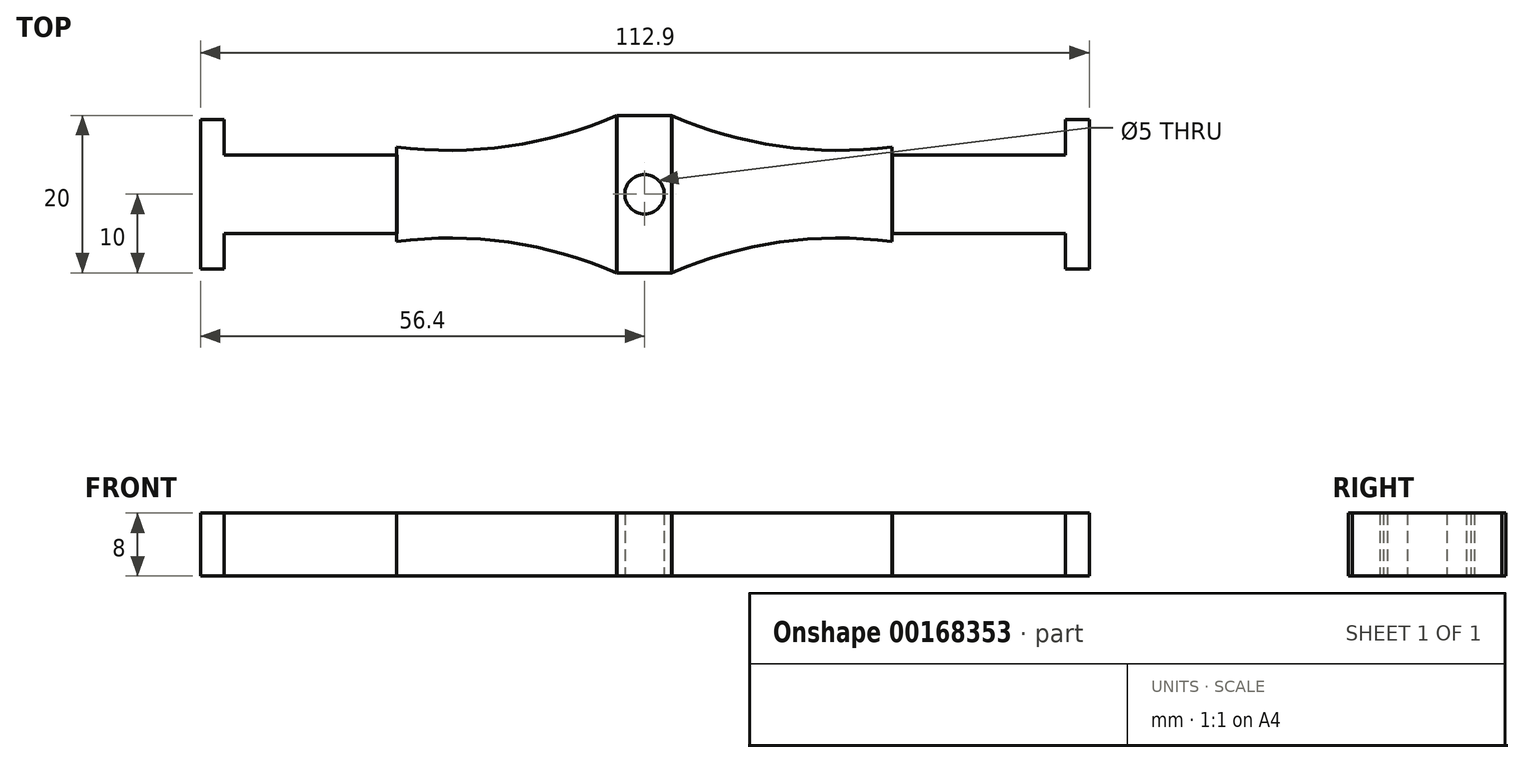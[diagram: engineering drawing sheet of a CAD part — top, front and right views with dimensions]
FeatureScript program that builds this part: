
annotation { "Feature Type Name" : "Feature", "Feature Type Description" : "" }
export const myFeature = defineFeature(function(context is Context, id is Id, definition is map)
    precondition{}
    {
        {
            var Q0;
            Q0=qCreatedBy(makeId("Top.planeOp"),FACE);
            var sketch = newSketch(context, id + "F0", { "sketchPlane" : qUnion([Q0])});
            skLineSegment(sketch, "E0.bottom", {"start": v(-3.5, 10) * mm, "end": v(3.5, 10) * mm});
            skLineSegment(sketch, "E0.top", {"start": v(-3.5, -10) * mm, "end": v(3.5, -10) * mm});
            skLineSegment(sketch, "E0.left", {"start": v(-3.5, 10) * mm, "end": v(-3.5, -10) * mm});
            skLineSegment(sketch, "E0.right", {"start": v(3.5, 10) * mm, "end": v(3.5, -10) * mm});
            skPoint(sketch, "E0.middle", {"position": v(0, 0) * mm});
            skLineSegment(sketch, "E1.bottom", {"start": v(-56.5, 9.5) * mm, "end": v(-53.5, 9.5) * mm});
            skLineSegment(sketch, "E1.top", {"start": v(-56.5, -9.5) * mm, "end": v(-53.5, -9.5) * mm});
            skLineSegment(sketch, "E1.left", {"start": v(-56.5, 9.5) * mm, "end": v(-56.5, -9.5) * mm});
            skLineSegment(sketch, "E1.right", {"start": v(-53.5, 9.5) * mm, "end": v(-53.5, -9.5) * mm});
            skPoint(sketch, "E1.middle", {"position": v(-55, 0) * mm});
            skLineSegment(sketch, "E2.left", {"start": v(-53.5, 4.03) * mm, "end": v(-53.5, -5.02) * mm});
            skLineSegment(sketch, "E3.bottom", {"start": v(-53.5, -5.02) * mm, "end": v(-31.5, -5.02) * mm});
            skLineSegment(sketch, "E3.top", {"start": v(-53.5, 4.98) * mm, "end": v(-31.5, 4.98) * mm});
            skLineSegment(sketch, "E3.left", {"start": v(-53.5, -5.02) * mm, "end": v(-53.5, 4.98) * mm});
            skLineSegment(sketch, "E3.right", {"start": v(-31.5, -5.02) * mm, "end": v(-31.5, 4.98) * mm});
            skLineSegment(sketch, "E4.MirrorCS", {"start": v(53.5, -5.02) * mm, "end": v(53.5, 4.98) * mm});
            skLineSegment(sketch, "E5.MirrorCS", {"start": v(53.5, 4.98) * mm, "end": v(31.5, 4.98) * mm});
            skLineSegment(sketch, "E6.MirrorCS", {"start": v(53.5, -5.02) * mm, "end": v(31.5, -5.02) * mm});
            skLineSegment(sketch, "E7.MirrorCS", {"start": v(31.5, -5.02) * mm, "end": v(31.5, 4.98) * mm});
            skCircle(sketch, "E8", {"center": v(0, 0) * mm, "radius": 2.5 * mm});
            skLineSegment(sketch, "E9", {"start": v(0, 24.62) * mm, "end": v(0, -21.09) * mm});
            skLineSegment(sketch, "E10.MirrorCS", {"start": v(53.5, 9.5) * mm, "end": v(53.5, -9.5) * mm});
            skLineSegment(sketch, "E11.MirrorCS", {"start": v(56.5, 9.5) * mm, "end": v(53.5, 9.5) * mm});
            skLineSegment(sketch, "E12.MirrorCS", {"start": v(56.5, 9.5) * mm, "end": v(56.5, -9.5) * mm});
            skLineSegment(sketch, "E13.MirrorCS", {"start": v(56.5, -9.5) * mm, "end": v(53.5, -9.5) * mm});
            skSolve(sketch);
        }
        {
            var Q0;
            Q0 = qSketchRegion(id + "F0", true);
            var Q1;
            {var subQ4=sQuery(id+"F0.wireOp",EDGE,"E3.bottom");Q1=makeQuery(id+"F0.imprint","IMPRINT",FACE,{"disambiguationData":[TD([[makeQuery(id+"F0.imprint","IMPRINT",EDGE,{"derivedFrom":subQ4}),1.0]])]});}
            extrude(context, id + "F1", {"entities" : qUnion([Q0, Q1]), "depth" : 8 * mm});
        }
        {
            var Q0;
            Q0=qCreatedBy(makeId("Top.planeOp"),FACE);
            var sketch = newSketch(context, id + "F2", { "sketchPlane" : qUnion([Q0])});
            skLineSegment(sketch, "E14", {"start": v(-31.51, 6) * mm, "end": v(-31.51, -6) * mm});
            skLineSegment(sketch, "E15", {"start": v(31.51, 6) * mm, "end": v(31.51, -6) * mm});
            skArc(sketch, "E16", {"start": v(-31.51, 6) * mm, "mid": v(-17.25, 6.1) * mm, "end": v(-3.54, 10) * mm});
            skPoint(sketch, "E17.endSnap0", {"position": v(31.51, 0) * mm});
            skArc(sketch, "E18.MirrorCS", {"start": v(-31.51, -6) * mm, "mid": v(-17.25, -6.1) * mm, "end": v(-3.54, -10) * mm});
            skArc(sketch, "E19.MirrorCS", {"start": v(31.51, 6) * mm, "mid": v(17.25, 6.1) * mm, "end": v(3.54, 10) * mm});
            skArc(sketch, "E20.MirrorCS", {"start": v(31.51, -6) * mm, "mid": v(17.25, -6.1) * mm, "end": v(3.54, -10) * mm});
            skLineSegment(sketch, "E21", {"start": v(-3.54, 10) * mm, "end": v(-3.54, -10) * mm});
            skLineSegment(sketch, "E22", {"start": v(3.54, 10) * mm, "end": v(3.54, -10) * mm});
            skSolve(sketch);
        }
        {
            var Q0;
            Q0=makeQuery(id+"F2.imprint","IMPRINT",FACE,{"disambiguationData":[TD([[makeQuery(id+"F2.imprint","IMPRINT",EDGE,{"derivedFrom":sQuery(id+"F2.wireOp",EDGE,"0frqyE8m-odSU-wRmI-uR99-W3MCcjVpDA67")}),-1.0]])]});
            var Q1;
            Q1=makeQuery(id+"F2.imprint","IMPRINT",FACE,{"disambiguationData":[TD([[makeQuery(id+"F2.imprint","IMPRINT",EDGE,{"derivedFrom":sQuery(id+"F2.wireOp",EDGE,"8dc07c38-c696-46b3-a4d5-0d6145278fd10.MirrorCS")}),-1.0]])]});
            var Q2;
            Q2=makeQuery(id+"F2.imprint","IMPRINT",FACE,{"disambiguationData":[TD([[makeQuery(id+"F2.imprint","IMPRINT",EDGE,{"derivedFrom":sQuery(id+"F2.wireOp",EDGE,"E14")}),1.0]])]});
            var Q3;
            Q3=makeQuery(id+"F2.imprint","IMPRINT",FACE,{"disambiguationData":[TD([[makeQuery(id+"F2.imprint","IMPRINT",EDGE,{"derivedFrom":sQuery(id+"F2.wireOp",EDGE,"E15")}),-1.0]])]});
            extrude(context, id + "F3", {"entities" : qUnion([Q0, Q1, Q2, Q3]), "depth" : 8 * mm});
        }
        {
            var Q0;
            Q0=qCreatedBy(makeId("Top.planeOp"),FACE);
            var sketch = newSketch(context, id + "F4", { "sketchPlane" : qUnion([Q0])});
            skLineSegment(sketch, "E23", {"start": v(-67.24, 0) * mm, "end": v(62.19, 0) * mm});
            skSolve(sketch);
        }
        {
            var Q0;
            Q0=makeQuery(id+"F1.opExtrude","SWEPT_BODY",BODY,{"disambiguationData":[OSD([sQuery(id+"F0.wireOp",EDGE,"E1.bottom"),sQuery(id+"F0.wireOp",EDGE,"E1.top"),sQuery(id+"F0.wireOp",EDGE,"E1.left"),sQuery(id+"F0.wireOp",EDGE,"E1.right"),sQuery(id+"F0.wireOp",EDGE,"E3.bottom"),sQuery(id+"F0.wireOp",EDGE,"E3.top"),sQuery(id+"F0.wireOp",EDGE,"E3.right")])]});
            var Q1;
            Q1=sQuery(id+"F4.wireOp",EDGE,"E23");
            var Q2;
            Q2=sQuery(id+"F4.wireOp",EDGE,"E23");
            transform(context, id + "F5", {"entities" : qUnion([Q0]), "transformType" : TransformType.TRANSLATION_DISTANCE, "transformDirection" : qUnion([Q2]), "distance" : 0.1 * mm, "makeCopy" : false});
        }
        {
            var Q0;
            Q0=makeQuery(id+"F3.opExtrude","SWEPT_BODY",BODY,{"disambiguationData":[OSD([sQuery(id+"F2.wireOp",EDGE,"E15"),sQuery(id+"F2.wireOp",EDGE,"E19.MirrorCS"),sQuery(id+"F2.wireOp",EDGE,"E20.MirrorCS"),sQuery(id+"F2.wireOp",EDGE,"E22")])]});
            var Q1;
            Q1=sQuery(id+"F4.wireOp",EDGE,"E23");
            var Q2;
            Q2=sQuery(id+"F4.wireOp",EDGE,"E23");
            transform(context, id + "F6", {"entities" : qUnion([Q0]), "transformType" : TransformType.TRANSLATION_DISTANCE, "transformDirection" : qUnion([Q2]), "distance" : 0.1 * mm, "oppositeDirection" : true, "makeCopy" : false});
        }
    });
